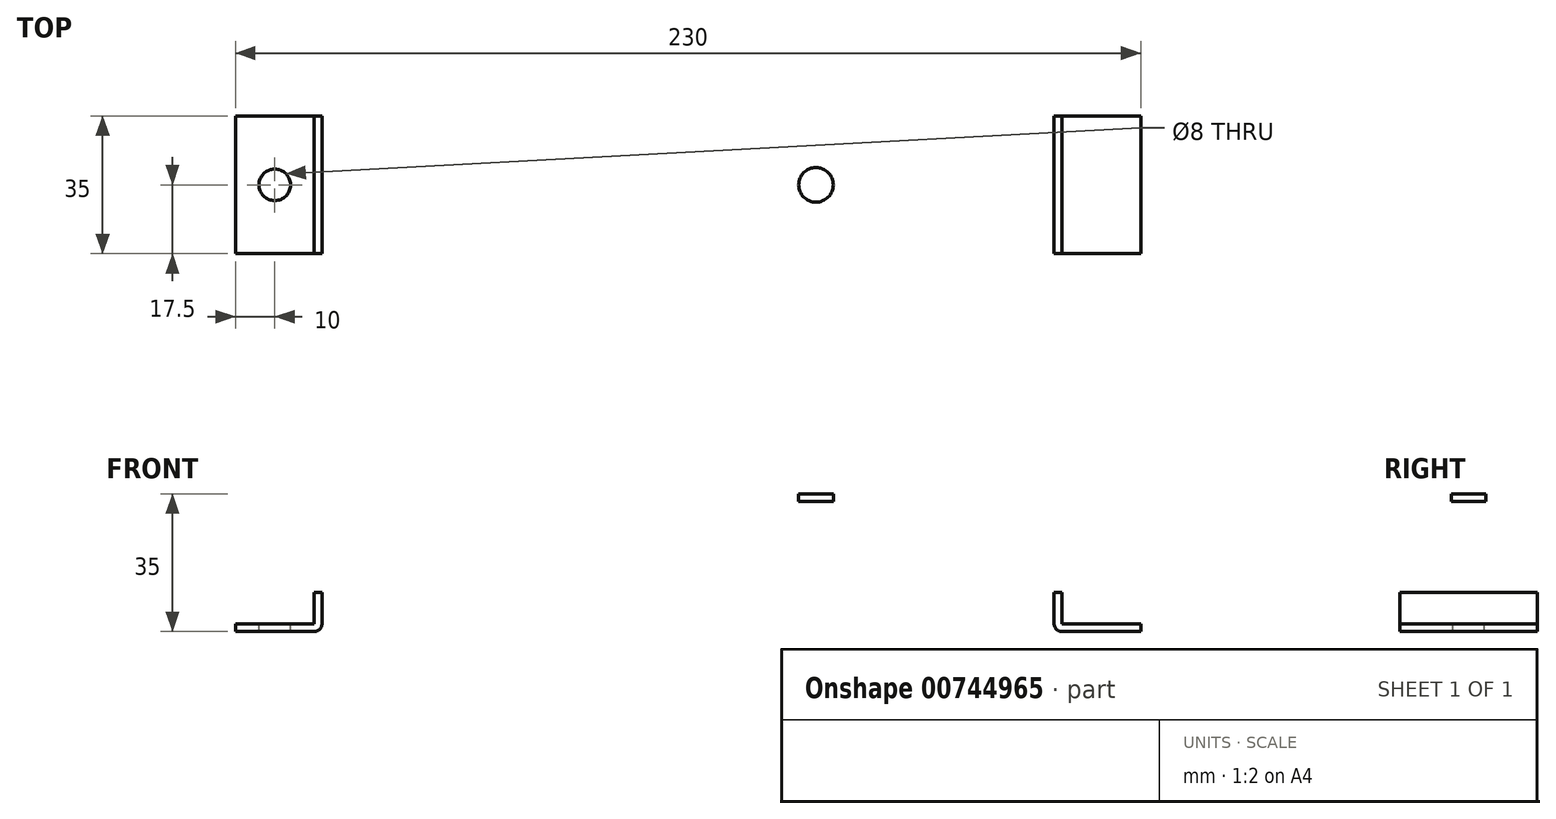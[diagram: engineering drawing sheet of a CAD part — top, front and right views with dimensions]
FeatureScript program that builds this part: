
annotation { "Feature Type Name" : "Feature", "Feature Type Description" : "" }
export const myFeature = defineFeature(function(context is Context, id is Id, definition is map)
    precondition{}
    {
        {
            var Q0;
            Q0=qCreatedBy(makeId("Front.planeOp"),FACE);
            var sketch = newSketch(context, id + "F0", { "sketchPlane" : qUnion([Q0])});
            skLineSegment(sketch, "E0.bottom", {"start": v(95, -5) * mm, "end": v(-95, -5) * mm});
            skLineSegment(sketch, "E0.left", {"start": v(95, -5) * mm, "end": v(95, -38) * mm});
            skLineSegment(sketch, "E0.right", {"start": v(-95, -5) * mm, "end": v(-95, -38) * mm});
            skLineSegment(sketch, "E1.bottom", {"start": v(-93, -40) * mm, "end": v(-115, -40) * mm});
            skLineSegment(sketch, "E1.top", {"start": v(-95, -38) * mm, "end": v(-115, -38) * mm});
            skLineSegment(sketch, "E1.right", {"start": v(-115, -40) * mm, "end": v(-115, -38) * mm});
            skLineSegment(sketch, "E2.MirrorCS", {"start": v(95, -38) * mm, "end": v(115, -38) * mm});
            skLineSegment(sketch, "E3.MirrorCS", {"start": v(115, -40) * mm, "end": v(115, -38) * mm});
            skLineSegment(sketch, "E4.MirrorCS", {"start": v(93, -40) * mm, "end": v(115, -40) * mm});
            skLineSegment(sketch, "E5.bottom", {"start": v(93, -7) * mm, "end": v(-93, -7) * mm});
            skLineSegment(sketch, "E5.left", {"start": v(93, -7) * mm, "end": v(93, -40) * mm});
            skLineSegment(sketch, "E5.right", {"start": v(-93, -7) * mm, "end": v(-93, -40) * mm});
            skPoint(sketch, "E5.middle", {"position": v(0, 0) * mm});
            skSolve(sketch);
        }
        {
            var Q0;
            Q0=makeQuery(id+"F0.imprint","IMPRINT",FACE,{"disambiguationData":[TD([[makeQuery(id+"F0.imprint","IMPRINT",EDGE,{"derivedFrom":sQuery(id+"F0.wireOp",EDGE,"KYryMLYI-daS0-5E23-TXuT-T7hqRafUo6E8.bottom")}),1.0]])]});
            var Q1;
            Q1=makeQuery(id+"F0.imprint","IMPRINT",FACE,{"disambiguationData":[TD([[makeQuery(id+"F0.imprint","IMPRINT",EDGE,{"derivedFrom":sQuery(id+"F0.wireOp",EDGE,"E0.bottom")}),1.0]])]});
            extrude(context, id + "F1", {"entities" : qUnion([Q0, Q1]), "endBound" : BoundingType.SYMMETRIC, "depth" : 35 * mm, "offsetDistance" : 25 * mm});
        }
        {
            var Q0;
            Q0=makeQuery(id+"F1.opExtrude","SWEPT_FACE",FACE,{"disambiguationData":[OSD([sQuery(id+"F0.wireOp",EDGE,"E1.top")])]});
            var sketch = newSketch(context, id + "F2", { "sketchPlane" : qUnion([Q0])});
            skCircle(sketch, "E6", {"center": v(-105, 0) * mm, "radius": 4 * mm});
            skPoint(sketch, "E6.centerSnap0", {"position": v(-105, -17.5) * mm});
            skPoint(sketch, "E6.centerSnap1", {"position": v(-115, 0) * mm});
            skCircle(sketch, "E7.MirrorC", {"center": v(105, 0) * mm, "radius": 4 * mm});
            skSolve(sketch);
        }
        {
            var Q0;
            Q0=makeQuery(id+"F2.imprint","IMPRINT",FACE,{"disambiguationData":[TD([[makeQuery(id+"F2.imprint","IMPRINT",EDGE,{"derivedFrom":sQuery(id+"F2.wireOp",EDGE,"E6")}),1.0]])]});
            var Q1;
            Q1=makeQuery(id+"F2.imprint","IMPRINT",FACE,{"disambiguationData":[TD([[makeQuery(id+"F2.imprint","IMPRINT",EDGE,{"derivedFrom":sQuery(id+"F2.wireOp",EDGE,"E7.MirrorC")}),-1.0]])]});
            extrude(context, id + "F3", {"entities" : qUnion([Q0, Q1]), "operationType" : NewBodyOperationType.REMOVE, "oppositeDirection" : true, "depth" : 25 * mm, "offsetDistance" : 25 * mm});
        }
        {
            var Q0;
            Q0=makeQuery(id+"F1.opExtrude","SWEPT_FACE",FACE,{"disambiguationData":[OSD([sQuery(id+"F0.wireOp",EDGE,"E0.bottom")])]});
            var sketch = newSketch(context, id + "F4", { "sketchPlane" : qUnion([Q0])});
            skCircle(sketch, "E8", {"center": v(-32.5, 0) * mm, "radius": 4.4 * mm});
            skCircle(sketch, "E9.MirrorC", {"center": v(32.5, 0) * mm, "radius": 4.4 * mm});
            skSolve(sketch);
        }
        {
            var Q0;
            Q0=makeQuery(id+"F4.imprint","IMPRINT",FACE,{"disambiguationData":[TD([[makeQuery(id+"F4.imprint","IMPRINT",EDGE,{"derivedFrom":sQuery(id+"F4.wireOp",EDGE,"E8")}),1.0]])]});
            var Q1;
            Q1=makeQuery(id+"F4.imprint","IMPRINT",FACE,{"disambiguationData":[TD([[makeQuery(id+"F4.imprint","IMPRINT",EDGE,{"derivedFrom":sQuery(id+"F4.wireOp",EDGE,"E9.MirrorC")}),-1.0]])]});
            extrude(context, id + "F5", {"entities" : qUnion([Q0, Q1]), "operationType" : NewBodyOperationType.REMOVE, "oppositeDirection" : true, "depth" : 25 * mm, "offsetDistance" : 25 * mm});
        }
        {
            var Q0;
            Q0=makeQuery(id+"F1.opExtrude","SWEPT_EDGE",EDGE,{"disambiguationData":[OSD([sQuery(id+"F0.wireOp",EDGE,"E0.bottom"),sQuery(id+"F0.wireOp",EDGE,"E0.left")])]});
            var Q1;
            Q1=makeQuery(id+"F1.opExtrude","SWEPT_EDGE",EDGE,{"disambiguationData":[OSD([sQuery(id+"F0.wireOp",EDGE,"E0.bottom"),sQuery(id+"F0.wireOp",EDGE,"E0.right")])]});
            var Q2;
            Q2=makeQuery(id+"F1.opExtrude","SWEPT_EDGE",EDGE,{"disambiguationData":[OSD([sQuery(id+"F0.wireOp",EDGE,"E1.bottom"),sQuery(id+"F0.wireOp",EDGE,"E5.right")])]});
            var Q3;
            Q3=makeQuery(id+"F1.opExtrude","SWEPT_EDGE",EDGE,{"disambiguationData":[OSD([sQuery(id+"F0.wireOp",EDGE,"E4.MirrorCS"),sQuery(id+"F0.wireOp",EDGE,"E5.left")])]});
            fillet(context, id + "F6", {"entities" : qUnion([Q0, Q1, Q2, Q3]), "radius" : 2 * mm, "tangentPropagation" : true, "allowEdgeOverflow" : false});
        }
    });
